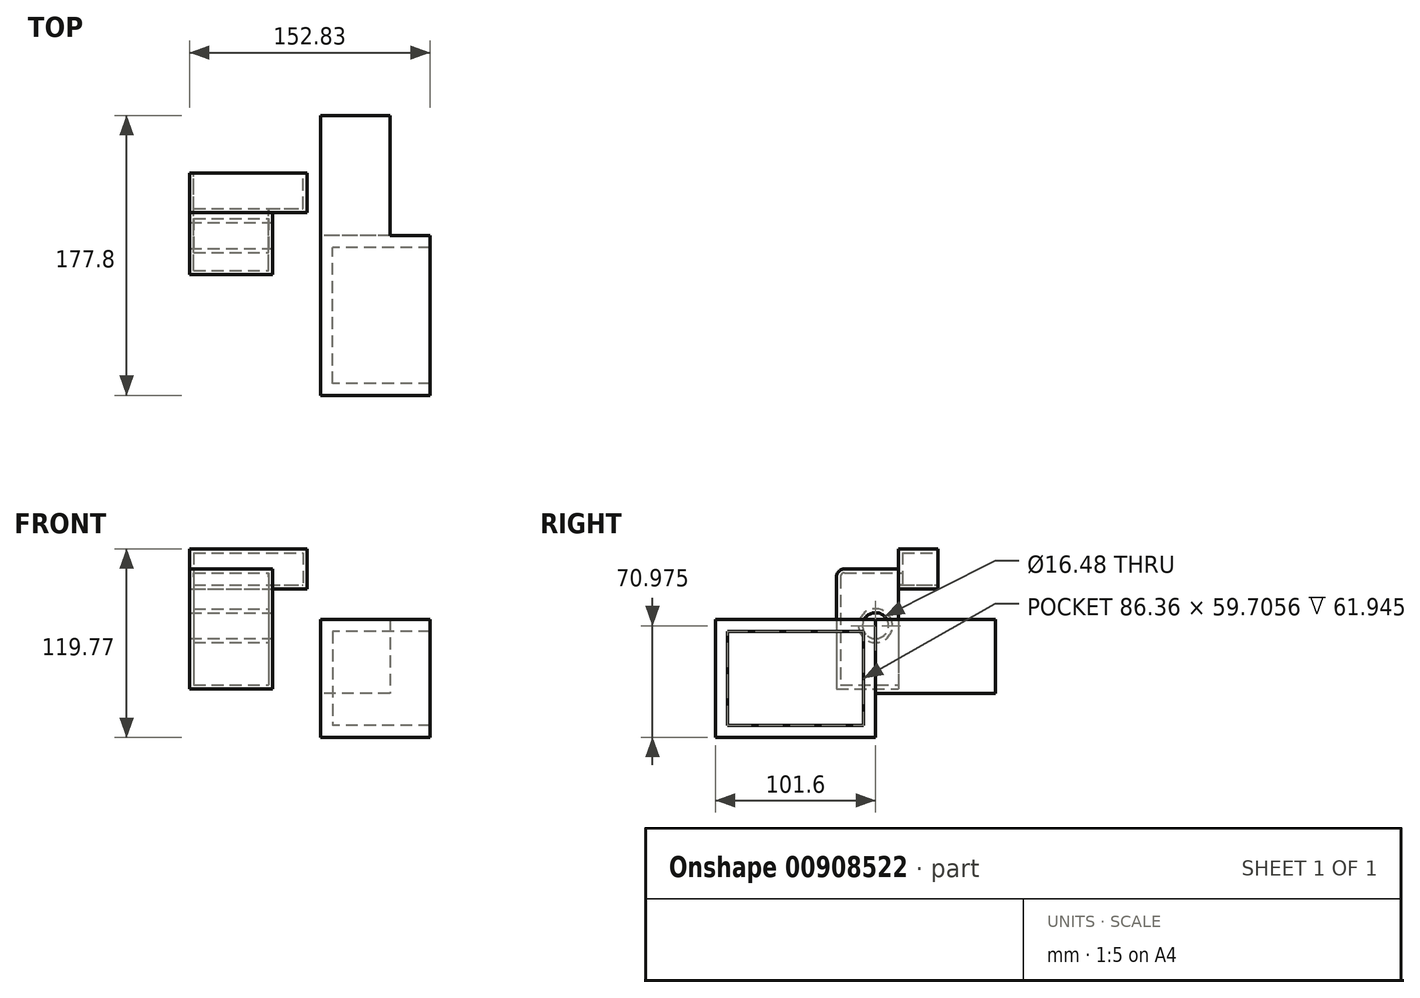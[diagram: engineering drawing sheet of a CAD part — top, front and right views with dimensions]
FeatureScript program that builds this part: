
annotation { "Feature Type Name" : "Feature", "Feature Type Description" : "" }
export const myFeature = defineFeature(function(context is Context, id is Id, definition is map)
    precondition{}
    {
        {
            var Q0;
            Q0=qCreatedBy(makeId("Top.planeOp"),FACE);
            var sketch = newSketch(context, id + "F0", { "sketchPlane" : qUnion([Q0])});
            skLineSegment(sketch, "E0.bottom", {"start": v(-95.6, -24.83) * mm, "end": v(-42.98, -24.83) * mm});
            skLineSegment(sketch, "E0.top", {"start": v(-95.6, 14.55) * mm, "end": v(-42.98, 14.55) * mm});
            skLineSegment(sketch, "E0.left", {"start": v(-95.6, -24.83) * mm, "end": v(-95.6, 14.55) * mm});
            skLineSegment(sketch, "E0.right", {"start": v(-42.98, -24.83) * mm, "end": v(-42.98, 14.55) * mm});
            skSolve(sketch);
        }
        {
            var Q0;
            Q0=makeQuery(id+"F0.imprint","IMPRINT",FACE,{"disambiguationData":[TD([[makeQuery(id+"F0.imprint","IMPRINT",EDGE,{"derivedFrom":sQuery(id+"F0.wireOp",EDGE,"E0.bottom")}),1.0]])]});
            extrude(context, id + "F1", {"entities" : qUnion([Q0]), "depth" : 76.2 * mm, "offsetDistance" : 25.4 * mm});
        }
        {
            var Q0;
            Q0=makeQuery(id+"F1.opExtrude","CAP_EDGE",EDGE,{"disambiguationData":[OSD([sQuery(id+"F0.wireOp",EDGE,"E0.bottom")])],"isStart":false});
            fillet(context, id + "F2", {"entities" : qUnion([Q0]), "radius" : 5.08 * mm, "tangentPropagation" : true, "allowEdgeOverflow" : false});
        }
        {
            var Q0;
            Q0=makeQuery(id+"F1.opExtrude","SWEPT_FACE",FACE,{"disambiguationData":[OSD([sQuery(id+"F0.wireOp",EDGE,"E0.right")])]});
            var sketch = newSketch(context, id + "F3", { "sketchPlane" : qUnion([Q0])});
            skCircle(sketch, "E1", {"center": v(0, 40.1) * mm, "radius": 8.24 * mm});
            skSolve(sketch);
        }
        {
            var Q0;
            Q0=makeQuery(id+"F3.imprint","IMPRINT",FACE,{"disambiguationData":[TD([[makeQuery(id+"F3.imprint","IMPRINT",EDGE,{"derivedFrom":sQuery(id+"F3.wireOp",EDGE,"E1")}),1.0]])]});
            extrude(context, id + "F4", {"entities" : qUnion([Q0]), "operationType" : NewBodyOperationType.REMOVE, "endBound" : BoundingType.THROUGH_ALL, "oppositeDirection" : true, "depth" : 25.4 * mm, "offsetDistance" : 25.4 * mm});
        }
        {
            var Q0;
            Q0=makeQuery(id+"F1.opExtrude","CAP_FACE",FACE,{"disambiguationData":[OSD([sQuery(id+"F0.wireOp",EDGE,"E0.bottom"),sQuery(id+"F0.wireOp",EDGE,"E0.top"),sQuery(id+"F0.wireOp",EDGE,"E0.left"),sQuery(id+"F0.wireOp",EDGE,"E0.right")])],"isStart":false});
            var sketch = newSketch(context, id + "F5", { "sketchPlane" : qUnion([Q0])});
            skLineSegment(sketch, "E2.bottom", {"start": v(-95.6, 14.55) * mm, "end": v(-20.87, 14.55) * mm});
            skLineSegment(sketch, "E2.top", {"start": v(-95.6, 39.72) * mm, "end": v(-20.87, 39.72) * mm});
            skLineSegment(sketch, "E2.left", {"start": v(-95.6, 14.55) * mm, "end": v(-95.6, 39.72) * mm});
            skLineSegment(sketch, "E2.right", {"start": v(-20.87, 14.55) * mm, "end": v(-20.87, 39.72) * mm});
            skSolve(sketch);
        }
        {
            var Q0;
            Q0=makeQuery(id+"F5.imprint","IMPRINT",FACE,{"disambiguationData":[TD([[makeQuery(id+"F5.imprint","IMPRINT",EDGE,{"derivedFrom":sQuery(id+"F5.wireOp",EDGE,"E2.top")}),-1.0]])]});
            extrude(context, id + "F6", {"entities" : qUnion([Q0]), "operationType" : NewBodyOperationType.ADD, "endBound" : BoundingType.SYMMETRIC, "depth" : 25.4 * mm, "offsetDistance" : 25.4 * mm});
        }
        {
            var Q0;
            Q0=makeQuery(id+"F6.opExtrude","SWEPT_FACE",FACE,{"disambiguationData":[OSD([sQuery(id+"F5.wireOp",EDGE,"E2.top")])]});
            var Q1;
            Q1=makeQuery(id+"F1.opExtrude","SWEPT_FACE",FACE,{"disambiguationData":[OSD([sQuery(id+"F0.wireOp",EDGE,"E0.top")])]});
            shell(context, id + "F7", {"entities" : qUnion([Q0, Q1]), "thickness" : 2.54 * mm});
        }
        {
            var Q0;
            Q0=qCreatedBy(makeId("Front.planeOp"),FACE);
            var sketch = newSketch(context, id + "F8", { "sketchPlane" : qUnion([Q0])});
            skLineSegment(sketch, "E3.bottom", {"start": v(57.23, 44.07) * mm, "end": v(-12.33, 44.07) * mm});
            skLineSegment(sketch, "E3.top", {"start": v(57.23, -30.87) * mm, "end": v(-12.33, -30.87) * mm});
            skLineSegment(sketch, "E3.left", {"start": v(57.23, 44.07) * mm, "end": v(57.23, -30.87) * mm});
            skLineSegment(sketch, "E3.right", {"start": v(-12.33, 44.07) * mm, "end": v(-12.33, -30.87) * mm});
            skSolve(sketch);
        }
        {
            var Q0;
            Q0=makeQuery(id+"F8.imprint","IMPRINT",FACE,{"disambiguationData":[TD([[makeQuery(id+"F8.imprint","IMPRINT",EDGE,{"derivedFrom":sQuery(id+"F8.wireOp",EDGE,"E3.bottom")}),1.0]])]});
            extrude(context, id + "F9", {"entities" : qUnion([Q0]), "depth" : 101.6 * mm, "offsetDistance" : 25.4 * mm});
        }
        {
            var Q0;
            Q0=makeQuery(id+"F9.opExtrude","SWEPT_FACE",FACE,{"disambiguationData":[OSD([sQuery(id+"F8.wireOp",EDGE,"E3.left")])]});
            shell(context, id + "F10", {"entities" : qUnion([Q0]), "thickness" : 7.62 * mm});
        }
        {
            var Q0;
            Q0=makeQuery(id+"F9.opExtrude","CAP_FACE",FACE,{"disambiguationData":[OSD([sQuery(id+"F8.wireOp",EDGE,"E3.bottom"),sQuery(id+"F8.wireOp",EDGE,"E3.top"),sQuery(id+"F8.wireOp",EDGE,"E3.left"),sQuery(id+"F8.wireOp",EDGE,"E3.right")])],"isStart":true});
            var sketch = newSketch(context, id + "F11", { "sketchPlane" : qUnion([Q0])});
            skLineSegment(sketch, "E4", {"start": v(12.33, 44.07) * mm, "end": v(-31.68, 44.07) * mm});
            skLineSegment(sketch, "E5", {"start": v(-31.68, 44.07) * mm, "end": v(-31.68, -2.85) * mm});
            skLineSegment(sketch, "E6", {"start": v(-31.68, -2.85) * mm, "end": v(12.33, -2.85) * mm});
            skLineSegment(sketch, "E7", {"start": v(12.33, -2.85) * mm, "end": v(12.33, 44.07) * mm});
            skSolve(sketch);
        }
        {
            var Q0;
            Q0=makeQuery(id+"F11.imprint","IMPRINT",FACE,{"disambiguationData":[TD([[makeQuery(id+"F11.imprint","IMPRINT",EDGE,{"derivedFrom":sQuery(id+"F11.wireOp",EDGE,"E4")}),-1.0]])]});
            extrude(context, id + "F12", {"entities" : qUnion([Q0]), "operationType" : NewBodyOperationType.ADD, "depth" : 76.2 * mm, "offsetDistance" : 25.4 * mm});
        }
    });
